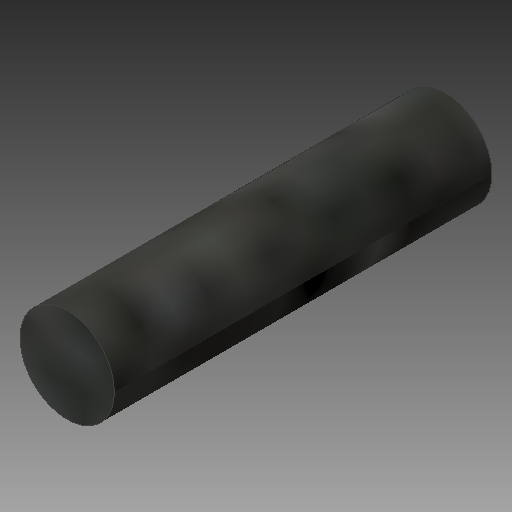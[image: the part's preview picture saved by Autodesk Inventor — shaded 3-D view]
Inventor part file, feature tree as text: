
AUTODESK INVENTOR PART (.ipt)
format: ipt  version: 2018 (Build 220112000, 112)  size: 110,080 bytes
history: native  units: mm
features: other x1, extrude x1, sketch x1
ambient origin geometry x8: Origin, YZ Plane, XZ Plane, XY Plane, X Axis, Y Axis, Z Axis, Center Point
bodies: Body1 (feature_tree)
feature tree (3):
  other  "ソリッド1"
  extrude  "押し出し1"  Depth=2.0mm
  sketch  "スケッチ1"
